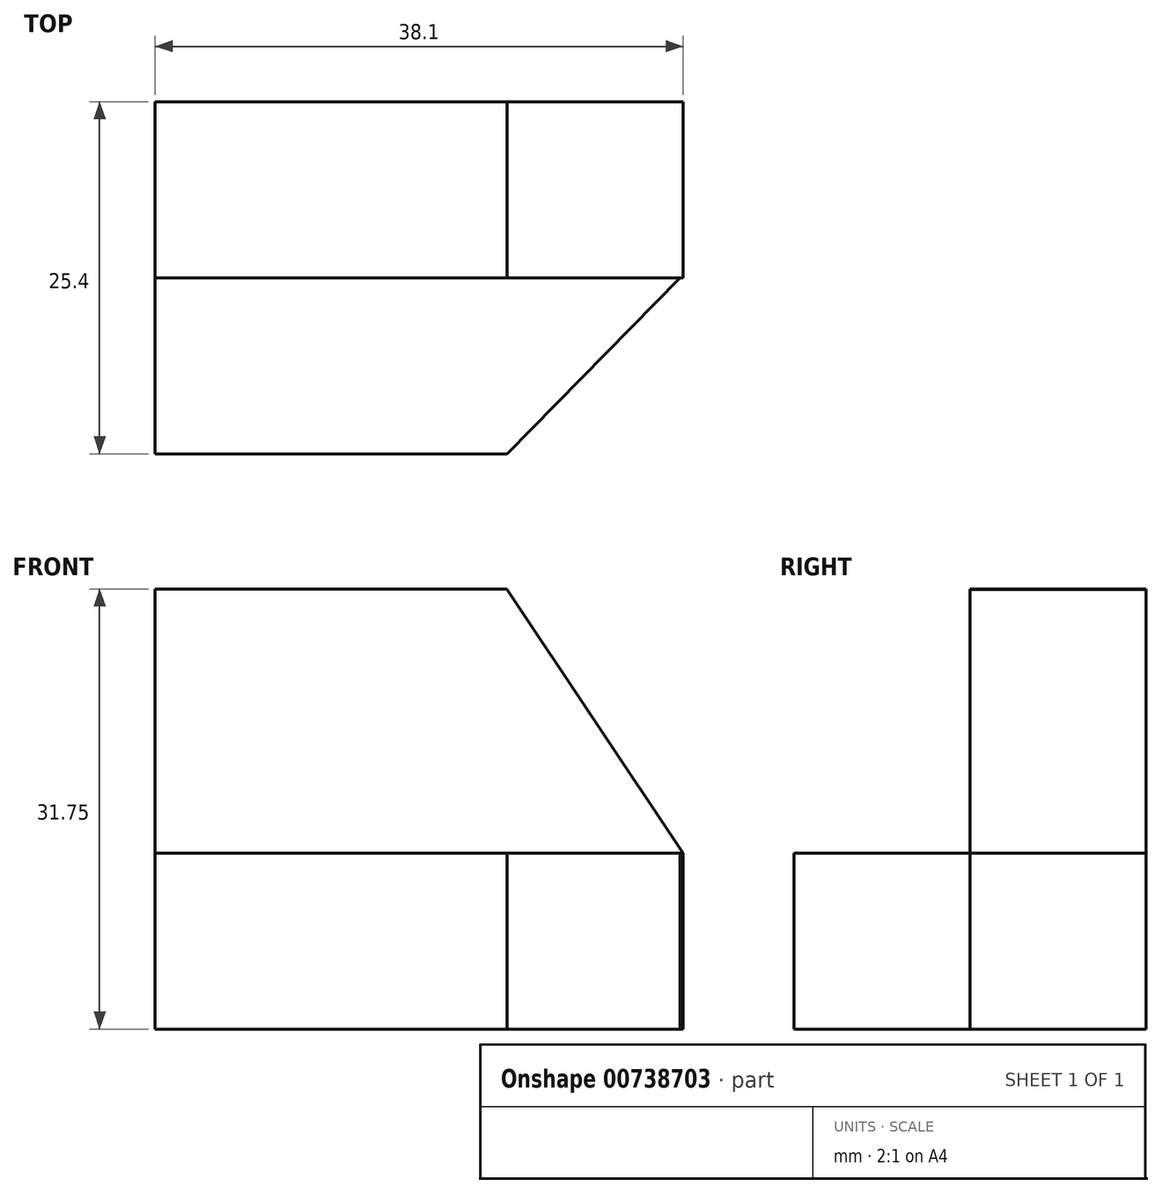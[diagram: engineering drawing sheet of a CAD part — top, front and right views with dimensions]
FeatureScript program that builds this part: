
annotation { "Feature Type Name" : "Feature", "Feature Type Description" : "" }
export const myFeature = defineFeature(function(context is Context, id is Id, definition is map)
    precondition{}
    {
        {
            var Q0;
            Q0=qCreatedBy(makeId("Right.planeOp"),FACE);
            var sketch = newSketch(context, id + "F0", { "sketchPlane" : qUnion([Q0])});
            skLineSegment(sketch, "E0", {"start": v(0, 0) * mm, "end": v(25.4, 0) * mm});
            skLineSegment(sketch, "E1", {"start": v(25.4, 0) * mm, "end": v(25.4, 31.75) * mm});
            skLineSegment(sketch, "E2", {"start": v(25.4, 31.75) * mm, "end": v(12.7, 31.75) * mm});
            skLineSegment(sketch, "E3", {"start": v(12.7, 31.75) * mm, "end": v(12.7, 12.7) * mm});
            skLineSegment(sketch, "E4", {"start": v(12.7, 12.7) * mm, "end": v(0, 12.7) * mm});
            skLineSegment(sketch, "E5", {"start": v(0, 12.7) * mm, "end": v(0, 0) * mm});
            skSolve(sketch);
        }
        {
            var Q0;
            Q0 = qSketchRegion(id + "F0", true);
            extrude(context, id + "F1", {"entities" : qUnion([Q0]), "depth" : 38.1 * mm, "offsetDistance" : 25.4 * mm});
        }
        {
            var Q0;
            Q0=qCreatedBy(makeId("Front.planeOp"),FACE);
            var sketch = newSketch(context, id + "F2", { "sketchPlane" : qUnion([Q0])});
            skLineSegment(sketch, "E6", {"start": v(25.4, 31.7) * mm, "end": v(38.1, 12.7) * mm});
            skLineSegment(sketch, "E7", {"start": v(38.1, 12.7) * mm, "end": v(38.1, 31.75) * mm});
            skLineSegment(sketch, "E8", {"start": v(38.1, 31.75) * mm, "end": v(25.4, 31.7) * mm});
            skSolve(sketch);
        }
        {
            var Q0;
            Q0 = qSketchRegion(id + "F2", true);
            extrude(context, id + "F3", {"entities" : qUnion([Q0]), "operationType" : NewBodyOperationType.REMOVE, "endBound" : BoundingType.THROUGH_ALL, "oppositeDirection" : true, "depth" : 25.4 * mm, "offsetDistance" : 25.4 * mm});
        }
        {
            var Q0;
            Q0=qCreatedBy(makeId("Front.planeOp"),FACE);
            var sketch = newSketch(context, id + "F4", { "sketchPlane" : qUnion([Q0])});
            skSolve(sketch);
        }
        {
            var Q0;
            Q0 = qSketchRegion(id + "F4", true);
            var Q1;
            Q1=makeQuery(id+"F3.boolean.opBoolean","COPY",FACE,{"derivedFrom":makeQuery(id+"F3.opExtrude","SWEPT_FACE",FACE,{"disambiguationData":[OSD([sQuery(id+"F2.wireOp",EDGE,"E8")])]})});
            extrude(context, id + "F5", {"entities" : qUnion([Q0, Q1]), "operationType" : NewBodyOperationType.REMOVE, "endBound" : BoundingType.THROUGH_ALL, "oppositeDirection" : true, "depth" : 25.4 * mm, "offsetDistance" : 25.4 * mm});
        }
        {
            var Q0;
            Q0=qCreatedBy(makeId("Top.planeOp"),FACE);
            var sketch = newSketch(context, id + "F6", { "sketchPlane" : qUnion([Q0])});
            skLineSegment(sketch, "E9", {"start": v(37.86, 12.69) * mm, "end": v(25.4, 0) * mm});
            skLineSegment(sketch, "E10", {"start": v(25.4, 0) * mm, "end": v(38.1, 0) * mm});
            skLineSegment(sketch, "E11", {"start": v(38.1, 0) * mm, "end": v(37.86, 12.69) * mm});
            skSolve(sketch);
        }
        {
            var Q0;
            Q0 = qSketchRegion(id + "F6", true);
            extrude(context, id + "F7", {"entities" : qUnion([Q0]), "operationType" : NewBodyOperationType.REMOVE, "endBound" : BoundingType.THROUGH_ALL, "depth" : 25.4 * mm, "offsetDistance" : 25.4 * mm});
        }
        {
            var Q0;
            Q0=qCreatedBy(makeId("Top.planeOp"),FACE);
            var sketch = newSketch(context, id + "F8", { "sketchPlane" : qUnion([Q0])});
            skSolve(sketch);
        }
        {
            var Q0;
            Q0 = qSketchRegion(id + "F8", true);
            var Q1;
            Q1=makeQuery(id+"F7.boolean.opBoolean","COPY",FACE,{"derivedFrom":makeQuery(id+"F7.opExtrude","SWEPT_FACE",FACE,{"disambiguationData":[OSD([sQuery(id+"F6.wireOp",EDGE,"E11")])]})});
            extrude(context, id + "F9", {"entities" : qUnion([Q0, Q1]), "operationType" : NewBodyOperationType.REMOVE, "endBound" : BoundingType.THROUGH_ALL, "oppositeDirection" : true, "depth" : 25.4 * mm, "offsetDistance" : 25.4 * mm});
        }
    });
